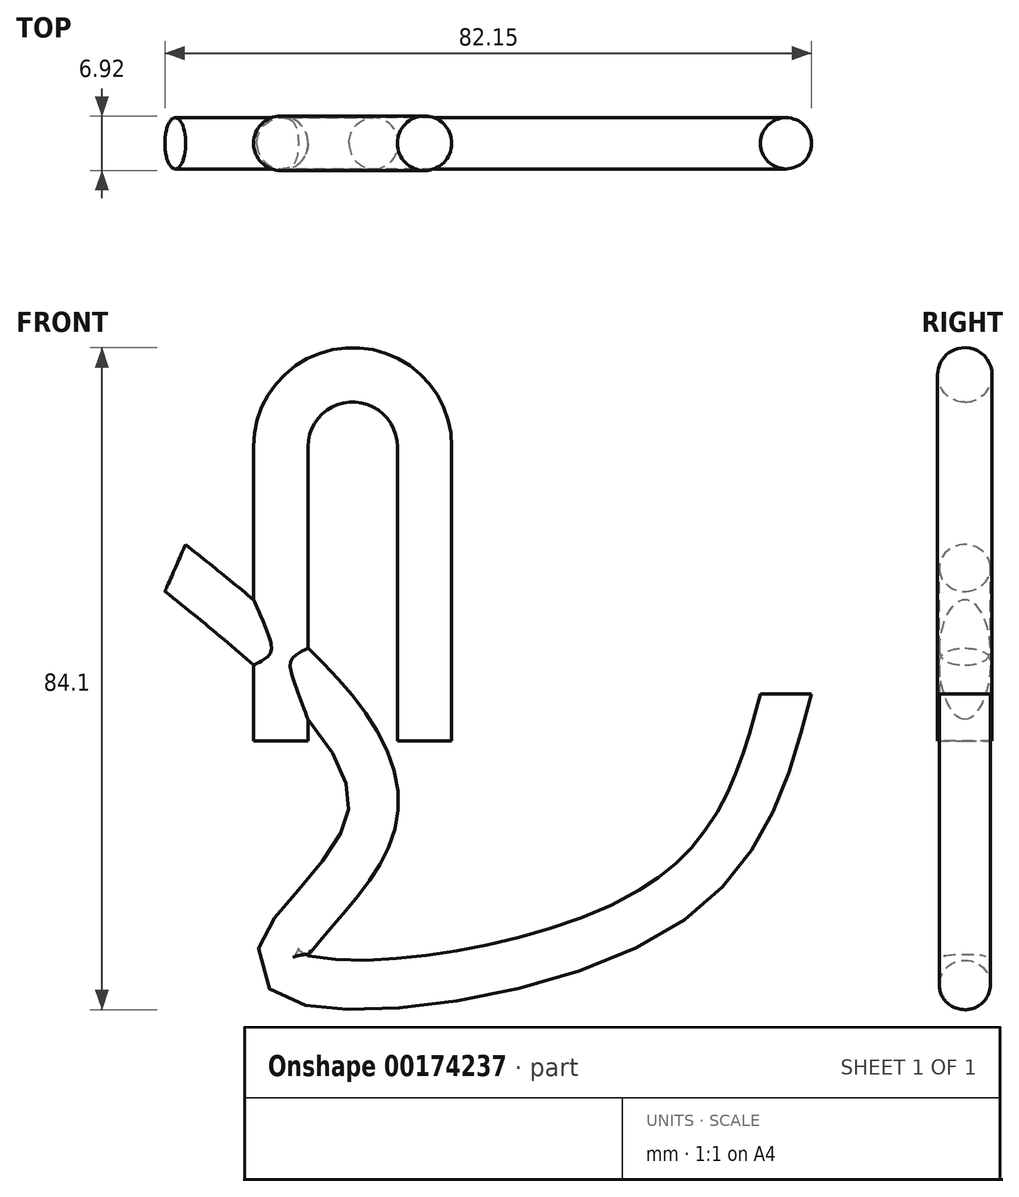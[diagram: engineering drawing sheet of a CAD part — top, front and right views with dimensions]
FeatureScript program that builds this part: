
annotation { "Feature Type Name" : "Feature", "Feature Type Description" : "" }
export const myFeature = defineFeature(function(context is Context, id is Id, definition is map)
    precondition{}
    {
        {
            var Q0;
            Q0=qCreatedBy(makeId("Front.planeOp"),FACE);
            var sketch = newSketch(context, id + "F0", { "sketchPlane" : qUnion([Q0])});
            skLineSegment(sketch, "E0.top", {"start": v(9.13, 18.68) * mm, "end": v(9.13, 18.68) * mm});
            skLineSegment(sketch, "E0.left", {"start": v(9.13, -18.68) * mm, "end": v(9.13, 18.68) * mm});
            skLineSegment(sketch, "E0.right", {"start": v(-9.13, -18.68) * mm, "end": v(-9.13, 18.68) * mm});
            skPoint(sketch, "E0.middle", {"position": v(0, 0) * mm});
            skArc(sketch, "E1", {"start": v(9.13, 18.68) * mm, "mid": v(0, 27.81) * mm, "end": v(-9.13, 18.68) * mm});
            skLineSegment(sketch, "E2.trimOffspring", {"start": v(-9.13, 18.68) * mm, "end": v(-9.13, 18.68) * mm});
            skSolve(sketch);
        }
        {
            var Q0;
            Q0=qCreatedBy(makeId("Top.planeOp"),FACE);
            var Q1;
            Q1=sQuery(id+"F0.wireOp",VERTEX,"E0.right.start");
            cPlane(context, id + "F1", {"entities" : qUnion([Q0, Q1]), "cplaneType" : CPlaneType.PLANE_POINT, "offset" : 25.4 * mm, "oppositeDirection" : true, "width" : 152.4 * mm, "height" : 152.4 * mm});
        }
        {
            var Q0;
            Q0=qCreatedBy(id+"F1.planeOp",FACE);
            var sketch = newSketch(context, id + "F2", { "sketchPlane" : qUnion([Q0])});
            skCircle(sketch, "E3", {"center": v(-9.13, 0) * mm, "radius": 3.46 * mm});
            skSolve(sketch);
        }
        {
            var Q0;
            Q0=makeQuery(id+"F2.imprint","IMPRINT",FACE,{"disambiguationData":[TD([[makeQuery(id+"F2.imprint","IMPRINT",EDGE,{"derivedFrom":sQuery(id+"F2.wireOp",EDGE,"E3")}),1.0]])]});
            var Q1;
            Q1=sQuery(id+"F0.wireOp",EDGE,"E0.right");
            var Q2;
            Q2=sQuery(id+"F0.wireOp",EDGE,"E1");
            var Q3;
            Q3=sQuery(id+"F0.wireOp",EDGE,"E0.left");
            sweep(context, id + "F3", {"profiles" : qUnion([Q0]), "path" : qUnion([Q1, Q2, Q3])});
        }
        {
            var Q0;
            Q0=qCreatedBy(makeId("Front.planeOp"),FACE);
            var sketch = newSketch(context, id + "F4", { "sketchPlane" : qUnion([Q0])});
            skFitSpline(sketch, "E4", {"points": [v(-22.53, 3.28) * mm, v(2.28, -29.24) * mm, v(-8.84, -47.2) * mm, v(36.51, -41.22) * mm, v(55.05, -12.7) * mm], "startDerivative": vector(152.77, -122.5) * mm, "endDerivative": vector(34.63, 130.8) * mm});
            skSolve(sketch);
        }
        {
            var Q0;
            Q0=qCreatedBy(id+"F1.planeOp",FACE);
            var Q1;
            Q1=sQuery(id+"F4.wireOp",VERTEX,"E4.4.internal");
            cPlane(context, id + "F5", {"entities" : qUnion([Q0, Q1]), "cplaneType" : CPlaneType.PLANE_POINT, "offset" : 25.4 * mm, "width" : 152.4 * mm, "height" : 152.4 * mm});
        }
        {
            var Q0;
            Q0=qCreatedBy(id+"F5.planeOp",FACE);
            var sketch = newSketch(context, id + "F6", { "sketchPlane" : qUnion([Q0])});
            skPoint(sketch, "E5.center.orphan", {"position": v(55.05, 0) * mm});
            skCircle(sketch, "E6", {"center": v(55.05, 0) * mm, "radius": 3.25 * mm});
            skSolve(sketch);
        }
        {
            var Q0;
            Q0=makeQuery(id+"F6.imprint","IMPRINT",FACE,{"disambiguationData":[TD([[makeQuery(id+"F6.imprint","IMPRINT",EDGE,{"derivedFrom":sQuery(id+"F6.wireOp",EDGE,"E6")}),1.0]])]});
            var Q1;
            Q1=sQuery(id+"F4.wireOp",EDGE,"E4");
            sweep(context, id + "F7", {"operationType" : NewBodyOperationType.ADD, "profiles" : qUnion([Q0]), "path" : qUnion([Q1])});
        }
    });
